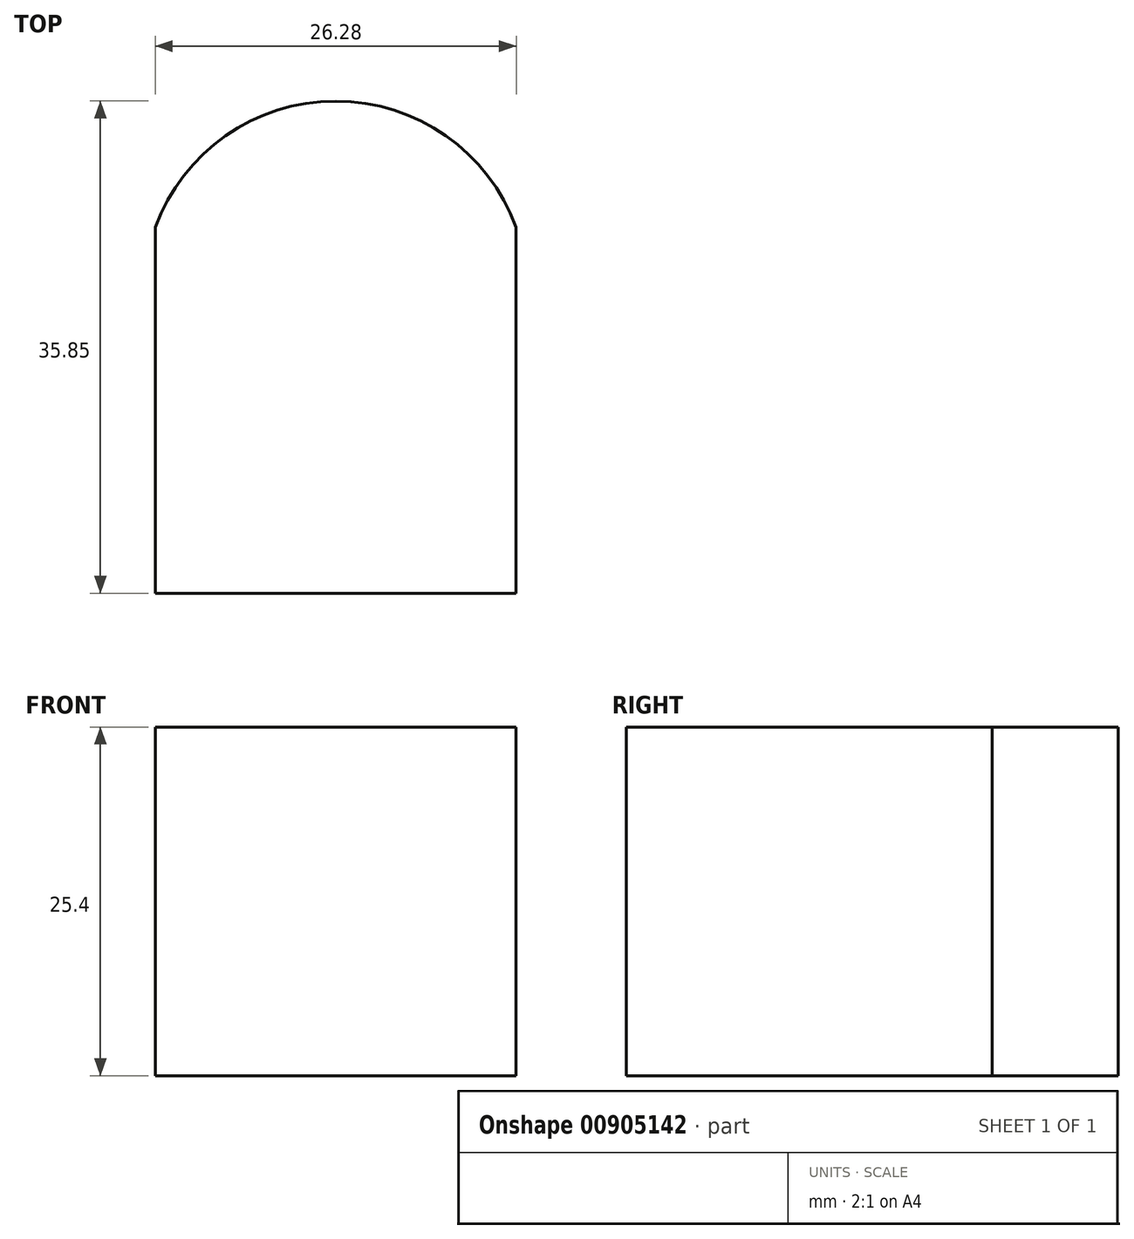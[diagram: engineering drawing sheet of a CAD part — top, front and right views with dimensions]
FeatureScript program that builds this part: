
annotation { "Feature Type Name" : "Feature", "Feature Type Description" : "" }
export const myFeature = defineFeature(function(context is Context, id is Id, definition is map)
    precondition{}
    {
        {
            var Q0;
            Q0=qCreatedBy(makeId("Top.planeOp"),FACE);
            var sketch = newSketch(context, id + "F0", { "sketchPlane" : qUnion([Q0])});
            skLineSegment(sketch, "E0.bottom", {"start": v(0, 0) * mm, "end": v(26.28, 0) * mm});
            skLineSegment(sketch, "E0.top", {"start": v(0, 26.65) * mm, "end": v(26.28, 26.65) * mm});
            skLineSegment(sketch, "E0.left", {"start": v(0, 0) * mm, "end": v(0, 26.65) * mm});
            skLineSegment(sketch, "E0.right", {"start": v(26.28, 0) * mm, "end": v(26.28, 26.65) * mm});
            skArc(sketch, "E1", {"start": v(26.28, 26.65) * mm, "mid": v(13.14, 35.85) * mm, "end": v(0, 26.65) * mm});
            skSolve(sketch);
        }
        {
            var Q0;
            Q0 = qSketchRegion(id + "F0", true);
            extrude(context, id + "F1", {"entities" : qUnion([Q0]), "depth" : 25.4 * mm, "offsetDistance" : 25.4 * mm});
        }
    });
